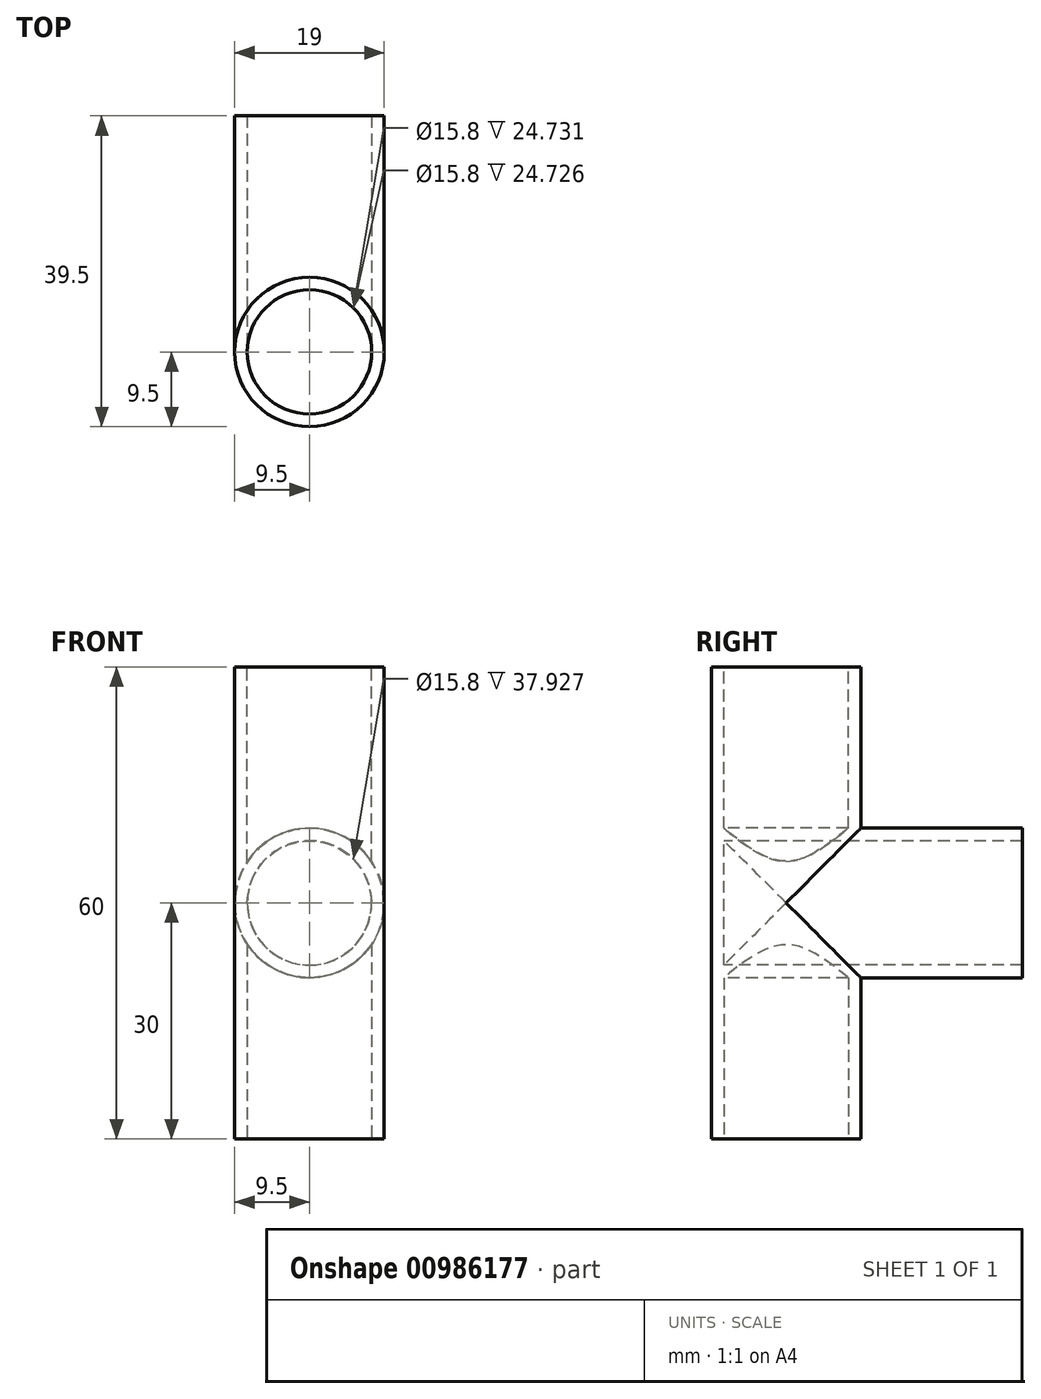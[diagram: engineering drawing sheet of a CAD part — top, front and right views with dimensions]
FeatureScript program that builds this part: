
annotation { "Feature Type Name" : "Feature", "Feature Type Description" : "" }
export const myFeature = defineFeature(function(context is Context, id is Id, definition is map)
    precondition{}
    {
        {
            var Q0;
            Q0=qCreatedBy(makeId("Front.planeOp"),FACE);
            var sketch = newSketch(context, id + "F0", { "sketchPlane" : qUnion([Q0])});
            skCircle(sketch, "E0", {"center": v(0, 0) * mm, "radius": 7.9 * mm});
            skCircle(sketch, "E1", {"center": v(0, 0) * mm, "radius": 9.5 * mm});
            skSolve(sketch);
        }
        {
            var Q0;
            Q0=qCreatedBy(makeId("Right.planeOp"),FACE);
            var sketch = newSketch(context, id + "F1", { "sketchPlane" : qUnion([Q0])});
            skLineSegment(sketch, "E2", {"start": v(-30, 0) * mm, "end": v(-30, 30) * mm});
            skLineSegment(sketch, "E3", {"start": v(-30, 0) * mm, "end": v(0, 0) * mm});
            skLineSegment(sketch, "E4", {"start": v(-30, 0) * mm, "end": v(-30, -30) * mm});
            skSolve(sketch);
        }
        {
            var Q0;
            Q0=makeQuery(id+"F0.imprint","IMPRINT",FACE,{"disambiguationData":[TD([[makeQuery(id+"F0.imprint","IMPRINT",EDGE,{"derivedFrom":sQuery(id+"F0.wireOp",EDGE,"E0")}),-1.0]])]});
            var Q1;
            Q1=sQuery(id+"F1.wireOp",EDGE,"E3");
            var Q2;
            Q2=sQuery(id+"F1.wireOp",EDGE,"E2");
            sweep(context, id + "F2", {"profiles" : qUnion([Q0]), "path" : qUnion([Q1, Q2])});
        }
        {
            var Q0;
            Q0=makeQuery(id+"F2.opSweep","SWEPT_BODY",BODY,{"disambiguationData":[OSD([sQuery(id+"F0.wireOp",EDGE,"E0"),sQuery(id+"F0.wireOp",EDGE,"E1"),sQuery(id+"F1.wireOp",EDGE,"E2")])]});
            var Q1;
            Q1=qCreatedBy(makeId("Top.planeOp"),FACE);
            mirror(context, id + "F3", {"operationType" : NewBodyOperationType.ADD, "entities" : qUnion([Q0]), "mirrorPlane" : qUnion([Q1])});
        }
    });
